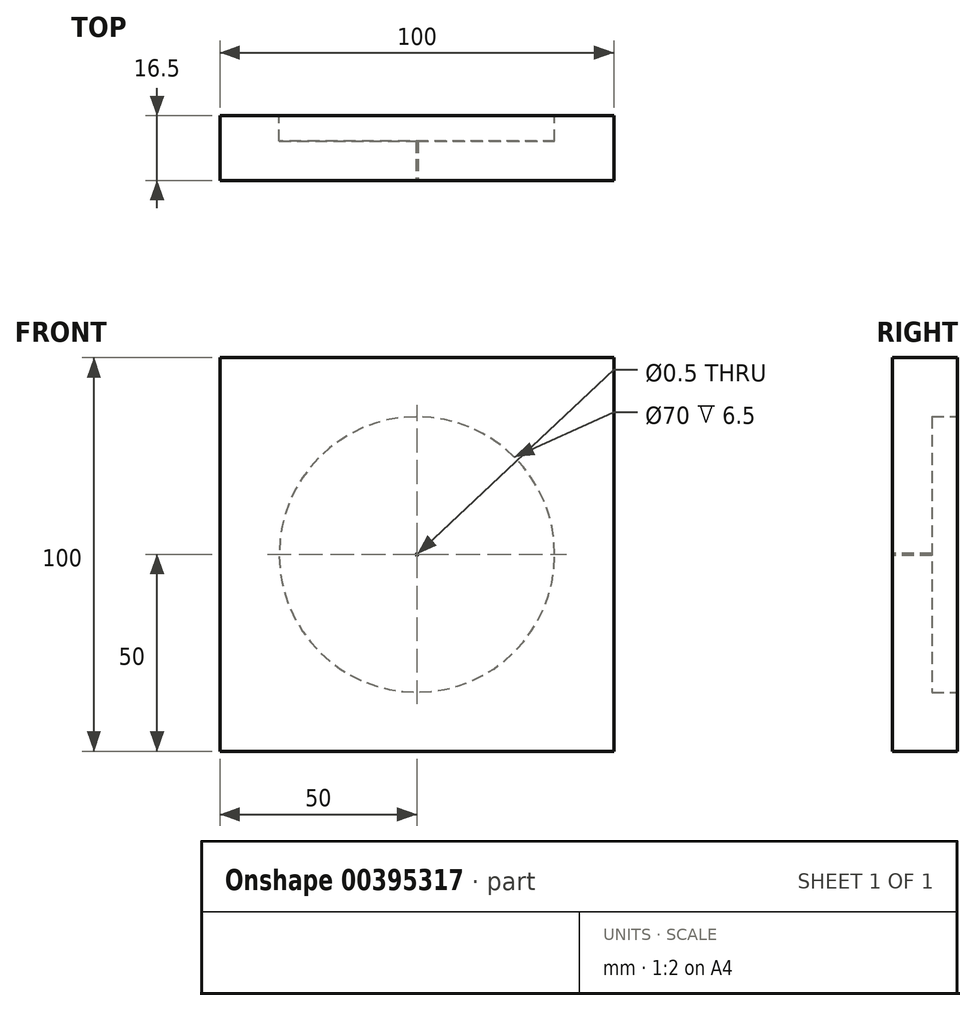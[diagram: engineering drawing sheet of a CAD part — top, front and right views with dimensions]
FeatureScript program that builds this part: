
annotation { "Feature Type Name" : "Feature", "Feature Type Description" : "" }
export const myFeature = defineFeature(function(context is Context, id is Id, definition is map)
    precondition{}
    {
        {
            var Q0;
            Q0=qCreatedBy(makeId("Front.planeOp"),FACE);
            var sketch = newSketch(context, id + "F0", { "sketchPlane" : qUnion([Q0])});
            skLineSegment(sketch, "E0.bottom", {"start": v(-50, 50) * mm, "end": v(50, 50) * mm});
            skLineSegment(sketch, "E0.top", {"start": v(-50, -50) * mm, "end": v(50, -50) * mm});
            skLineSegment(sketch, "E0.left", {"start": v(-50, 50) * mm, "end": v(-50, -50) * mm});
            skLineSegment(sketch, "E0.right", {"start": v(50, 50) * mm, "end": v(50, -50) * mm});
            skPoint(sketch, "E0.middle", {"position": v(0, 0) * mm});
            skSolve(sketch);
        }
        {
            var Q0;
            Q0=makeQuery(id+"F0.imprint","IMPRINT",FACE,{"disambiguationData":[TD([[makeQuery(id+"F0.imprint","IMPRINT",EDGE,{"derivedFrom":sQuery(id+"F0.wireOp",EDGE,"E0.bottom")}),-1.0]])]});
            extrude(context, id + "F1", {"entities" : qUnion([Q0]), "depth" : 16.5 * mm});
        }
        {
            var Q0;
            Q0=makeQuery(id+"F1.opExtrude","CAP_FACE",FACE,{"disambiguationData":[OSD([sQuery(id+"F0.wireOp",EDGE,"E0.bottom"),sQuery(id+"F0.wireOp",EDGE,"E0.top"),sQuery(id+"F0.wireOp",EDGE,"E0.left"),sQuery(id+"F0.wireOp",EDGE,"E0.right")])],"isStart":false});
            var sketch = newSketch(context, id + "F2", { "sketchPlane" : qUnion([Q0])});
            skCircle(sketch, "E1", {"center": v(0, 0) * mm, "radius": 0.25 * mm});
            skSolve(sketch);
        }
        {
            var Q0;
            Q0=makeQuery(id+"F2.imprint","IMPRINT",FACE,{"disambiguationData":[TD([[makeQuery(id+"F2.imprint","IMPRINT",EDGE,{"derivedFrom":sQuery(id+"F2.wireOp",EDGE,"E1")}),1.0]])]});
            extrude(context, id + "F3", {"entities" : qUnion([Q0]), "operationType" : NewBodyOperationType.REMOVE, "endBound" : BoundingType.THROUGH_ALL, "oppositeDirection" : true, "depth" : 25.4 * mm});
        }
        {
            var Q0;
            Q0=makeQuery(id+"F1.opExtrude","CAP_FACE",FACE,{"disambiguationData":[OSD([sQuery(id+"F0.wireOp",EDGE,"E0.bottom"),sQuery(id+"F0.wireOp",EDGE,"E0.top"),sQuery(id+"F0.wireOp",EDGE,"E0.left"),sQuery(id+"F0.wireOp",EDGE,"E0.right")])],"isStart":true});
            var sketch = newSketch(context, id + "F4", { "sketchPlane" : qUnion([Q0])});
            skCircle(sketch, "E2", {"center": v(0, 0) * mm, "radius": 35 * mm});
            skSolve(sketch);
        }
        {
            var Q0;
            Q0=makeQuery(id+"F4.imprint","IMPRINT",FACE,{"disambiguationData":[TD([[makeQuery(id+"F4.imprint","IMPRINT",EDGE,{"derivedFrom":makeQuery(id+"F3.boolean.opBoolean","INTERSECT",EDGE,{"derivedFrom":[makeQuery(id+"F1.opExtrude","CAP_FACE",FACE,{"disambiguationData":[OSD([sQuery(id+"F0.wireOp",EDGE,"E0.bottom"),sQuery(id+"F0.wireOp",EDGE,"E0.top"),sQuery(id+"F0.wireOp",EDGE,"E0.left"),sQuery(id+"F0.wireOp",EDGE,"E0.right")])],"isStart":true}),makeQuery(id+"F3.opExtrude","SWEPT_FACE",FACE,{"disambiguationData":[OSD([sQuery(id+"F2.wireOp",EDGE,"E1")])]})]})}),-1.0]])]});
            var Q1;
            Q1=makeQuery(id+"F4.imprint","IMPRINT",FACE,{"disambiguationData":[TD([[makeQuery(id+"F4.imprint","IMPRINT",EDGE,{"derivedFrom":sQuery(id+"F4.wireOp",EDGE,"E2")}),1.0]])]});
            extrude(context, id + "F5", {"entities" : qUnion([Q0, Q1]), "operationType" : NewBodyOperationType.REMOVE, "oppositeDirection" : true, "depth" : 6.5 * mm});
        }
    });
